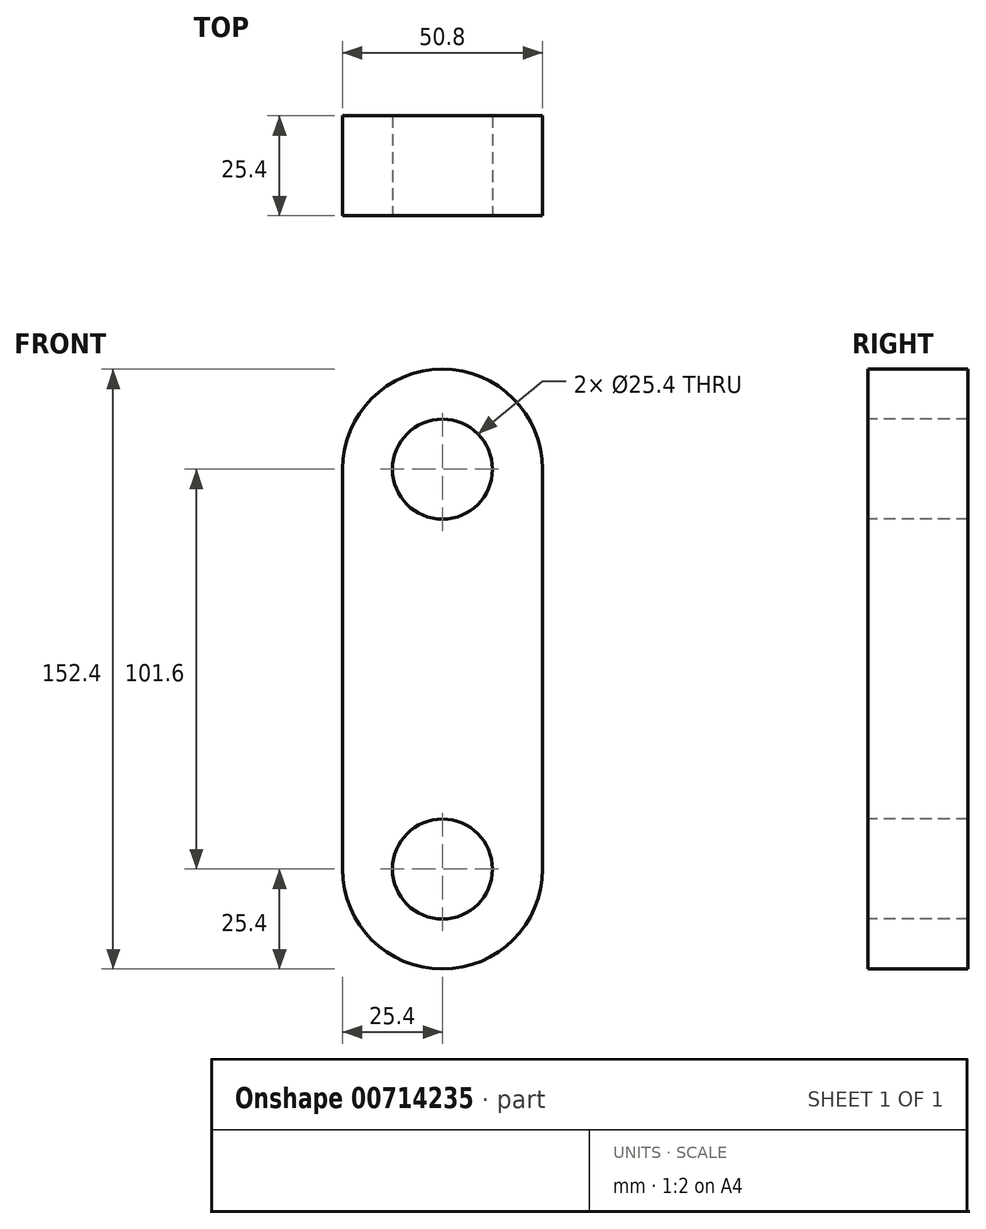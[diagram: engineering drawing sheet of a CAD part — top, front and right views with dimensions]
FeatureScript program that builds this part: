
annotation { "Feature Type Name" : "Feature", "Feature Type Description" : "" }
export const myFeature = defineFeature(function(context is Context, id is Id, definition is map)
    precondition{}
    {
        {
            var Q0;
            Q0=qCreatedBy(makeId("Front.planeOp"),FACE);
            var sketch = newSketch(context, id + "F0", { "sketchPlane" : qUnion([Q0])});
            skLineSegment(sketch, "E0.bottom", {"start": v(25.4, 0) * mm, "end": v(-25.4, 0) * mm});
            skLineSegment(sketch, "E0.top", {"start": v(25.4, 50.8) * mm, "end": v(-25.4, 50.8) * mm});
            skLineSegment(sketch, "E0.left", {"start": v(25.4, 0) * mm, "end": v(25.4, 50.8) * mm});
            skLineSegment(sketch, "E0.right", {"start": v(-25.4, 0) * mm, "end": v(-25.4, 50.8) * mm});
            skCircle(sketch, "E1", {"center": v(0, 50.8) * mm, "radius": 25.4 * mm});
            skSolve(sketch);
        }
        {
            var Q0;
            {var subQ0=sQuery(id+"F0.wireOp",EDGE,"E0.top");Q0=makeQuery(id+"F0.imprint","IMPRINT",FACE,{"disambiguationData":[TD([[makeQuery(id+"F0.imprint","IMPRINT",EDGE,{"derivedFrom":subQ0}),1.0]])]});}
            var Q1;
            {var subQ0=sQuery(id+"F0.wireOp",EDGE,"E0.top");Q1=makeQuery(id+"F0.imprint","IMPRINT",FACE,{"disambiguationData":[TD([[makeQuery(id+"F0.imprint","IMPRINT",EDGE,{"derivedFrom":subQ0}),-1.0]])]});}
            var Q2;
            Q2=makeQuery(id+"F0.imprint","IMPRINT",FACE,{"disambiguationData":[TD([[makeQuery(id+"F0.imprint","IMPRINT",EDGE,{"derivedFrom":sQuery(id+"F0.wireOp",EDGE,"E0.bottom")}),-1.0]])]});
            extrude(context, id + "F1", {"entities" : qUnion([Q0, Q1, Q2]), "depth" : 25.4 * mm, "offsetDistance" : 25.4 * mm});
        }
        {
            var Q0;
            Q0=makeQuery(id+"F1.opExtrude","CAP_FACE",FACE,{"disambiguationData":[OSD([sQuery(id+"F0.wireOp",EDGE,"E0.bottom"),sQuery(id+"F0.wireOp",EDGE,"E0.left"),sQuery(id+"F0.wireOp",EDGE,"E0.right"),sQuery(id+"F0.wireOp",EDGE,"E1")])],"isStart":false});
            var sketch = newSketch(context, id + "F2", { "sketchPlane" : qUnion([Q0])});
            skCircle(sketch, "E2", {"center": v(0, 50.8) * mm, "radius": 12.7 * mm});
            skSolve(sketch);
        }
        {
            var Q0;
            Q0=makeQuery(id+"F2.imprint","IMPRINT",FACE,{"disambiguationData":[TD([[makeQuery(id+"F2.imprint","IMPRINT",EDGE,{"derivedFrom":sQuery(id+"F2.wireOp",EDGE,"E2")}),1.0]])]});
            extrude(context, id + "F3", {"entities" : qUnion([Q0]), "operationType" : NewBodyOperationType.REMOVE, "oppositeDirection" : true, "depth" : 50.8 * mm, "offsetDistance" : 25.4 * mm});
        }
        {
            var Q0;
            Q0=makeQuery(id+"F1.opExtrude","SWEPT_BODY",BODY,{"disambiguationData":[OSD([sQuery(id+"F0.wireOp",EDGE,"E0.bottom"),sQuery(id+"F0.wireOp",EDGE,"E0.left"),sQuery(id+"F0.wireOp",EDGE,"E0.right"),sQuery(id+"F0.wireOp",EDGE,"E1")])]});
            var Q1;
            Q1=makeQuery(id+"F1.opExtrude","SWEPT_FACE",FACE,{"disambiguationData":[OSD([sQuery(id+"F0.wireOp",EDGE,"E0.bottom")])]});
            mirror(context, id + "F4", {"operationType" : NewBodyOperationType.ADD, "entities" : qUnion([Q0]), "mirrorPlane" : qUnion([Q1])});
        }
    });
